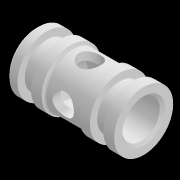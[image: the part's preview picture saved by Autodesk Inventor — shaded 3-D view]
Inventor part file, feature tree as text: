
AUTODESK INVENTOR PART (.ipt)
format: ipt  version: 2021 (Build 250183000, 183)  size: 208,896 bytes
history: native  units: mm
features: sketch x2, revolve x1, chamfer x1, plane x1, hole x1, pattern_circular x1, fillet x1
ambient origin geometry x8: Origin, YZ Plane, XZ Plane, XY Plane, X Axis, Y Axis, Z Axis, Center Point
bodies: Solid1 (feature_tree)
feature tree (8):
  revolve  "Revolution1"  [1 undecoded]
  chamfer  "Chamfer1"  Distance=10.0mm
  plane  "Work Plane1"
  hole  "Hole1"  [1 undecoded]
  pattern_circular  "Circular Pattern1"  [2 undecoded]
  fillet  "Fillet1"  Radius=6.0mm
  sketch  "Sketch2"  dims[d0=7.0mm d1=11.0mm]
  sketch  "Sketch3"  dims[d2=10.0mm d3=10.0mm d5=5.0mm d6=7.5mm d7=6.0mm d8=4.0mm d11=2.0mm d12=2.5mm d13=8.3mm d14=8.3mm d15=2.5mm d16=2.0mm d17=90.0deg d18=0.5mm d19=2.0mm d20=45.0deg d21=4.0mm d22=6.0mm d23=4.0mm d24=2.0mm d25=90.0deg d26=15.0mm d27=20.594885mm d28=40.0mm d29=360.0deg d31=7.0mm d32=0.5mm d33=0.5mm d34=0.65mm d35=2.0mm]
note: 4 required parameter values undecoded (feature->parameter linkage not recoverable at this tier; creation-order binding heuristic only, values carry confidence <= 0.55)